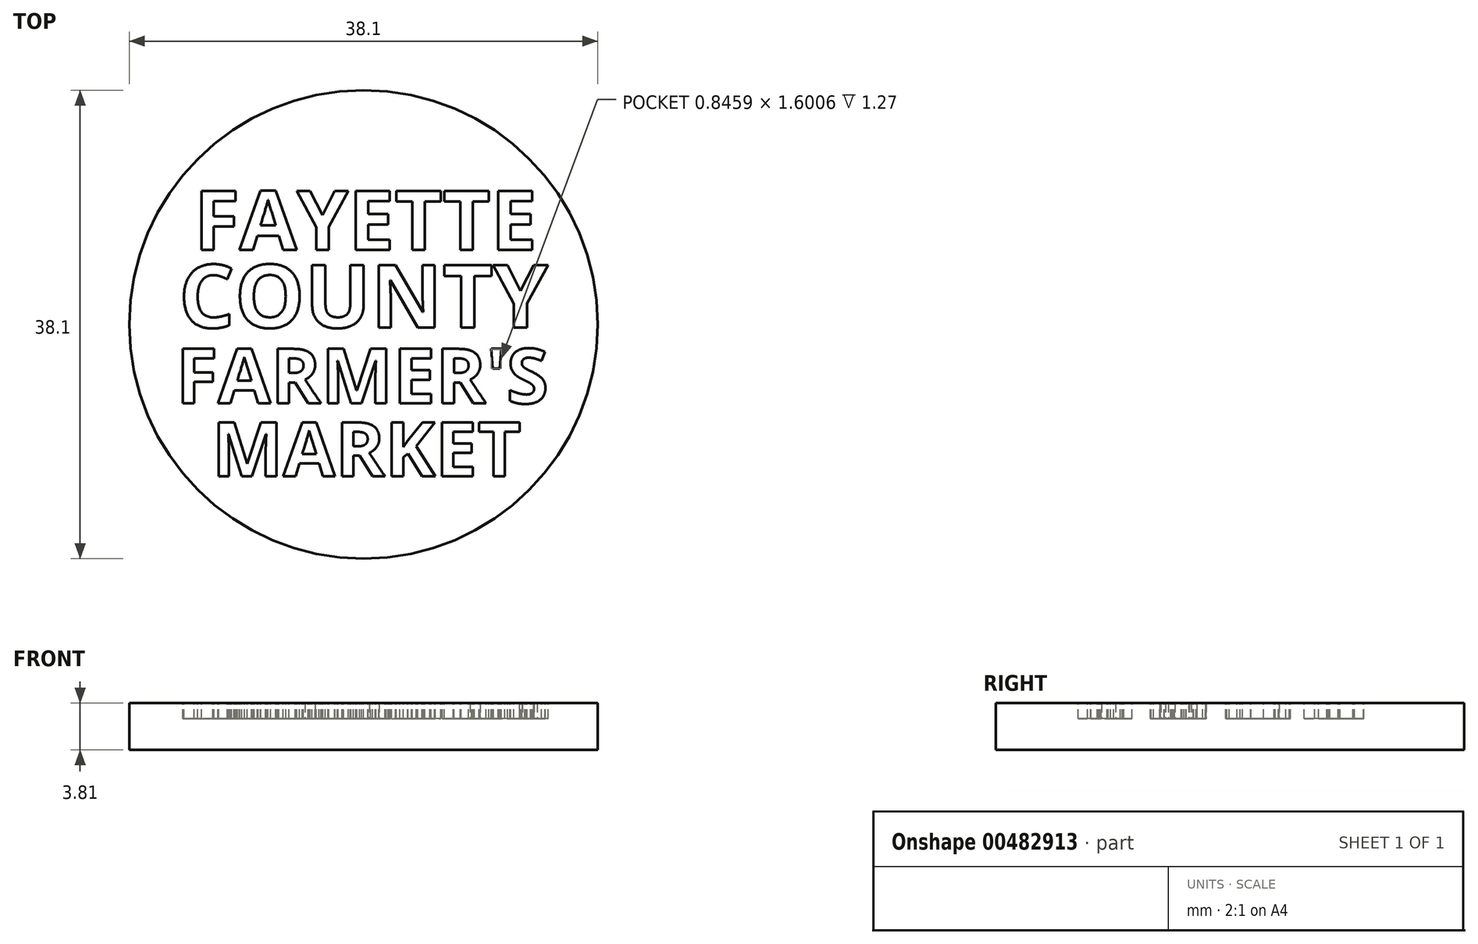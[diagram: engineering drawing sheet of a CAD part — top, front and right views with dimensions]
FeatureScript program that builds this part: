
annotation { "Feature Type Name" : "Feature", "Feature Type Description" : "" }
export const myFeature = defineFeature(function(context is Context, id is Id, definition is map)
    precondition{}
    {
        {
            var Q0;
            Q0=qCreatedBy(makeId("Top.planeOp"),FACE);
            var sketch = newSketch(context, id + "F0", { "sketchPlane" : qUnion([Q0])});
            skCircle(sketch, "E0", {"center": v(0, 0) * mm, "radius": 19.05 * mm});
            skSolve(sketch);
        }
        {
            var Q0;
            Q0 = qSketchRegion(id + "F0", true);
            extrude(context, id + "F1", {"entities" : qUnion([Q0]), "depth" : 3.8 * mm});
        }
        {
            var Q0;
            Q0=makeQuery(id+"F1.opExtrude","CAP_FACE",FACE,{"disambiguationData":[OSD([sQuery(id+"F0.wireOp",EDGE,"E0")])],"isStart":false});
            var sketch = newSketch(context, id + "F2", { "sketchPlane" : qUnion([Q0])});
            skText(sketch, "E1", { "text": "FAYETTE", "fontName": "OpenSans-Bold.ttf"});
            skText(sketch, "E2", { "text": "FARMER\'S", "fontName": "OpenSans-Bold.ttf"});
            skText(sketch, "E3", { "text": "MARKET", "fontName": "OpenSans-Bold.ttf"});
            skText(sketch, "E4", { "text": "COUNTY", "fontName": "OpenSans-Bold.ttf"});
            const initialGuessF2  = {"E1": [-0.01379, 0.00605, 1, 0, 0.00485], "E2": [-0.01525, -0.00642, 1, 0, 0.00447], "E3": [-0.01233, -0.01236, 1, 0, 0.00442], "E4": [-0.01502, -0.00026, 1, 0, 0.00514]};
            skSetInitialGuess(sketch, initialGuessF2);
            skSolve(sketch);
        }
        {
            var Q0;
            Q0 = qSketchRegion(id + "F2", true);
            extrude(context, id + "F3", {"entities" : qUnion([Q0]), "operationType" : NewBodyOperationType.REMOVE, "oppositeDirection" : true, "depth" : 1.27 * mm});
        }
    });
